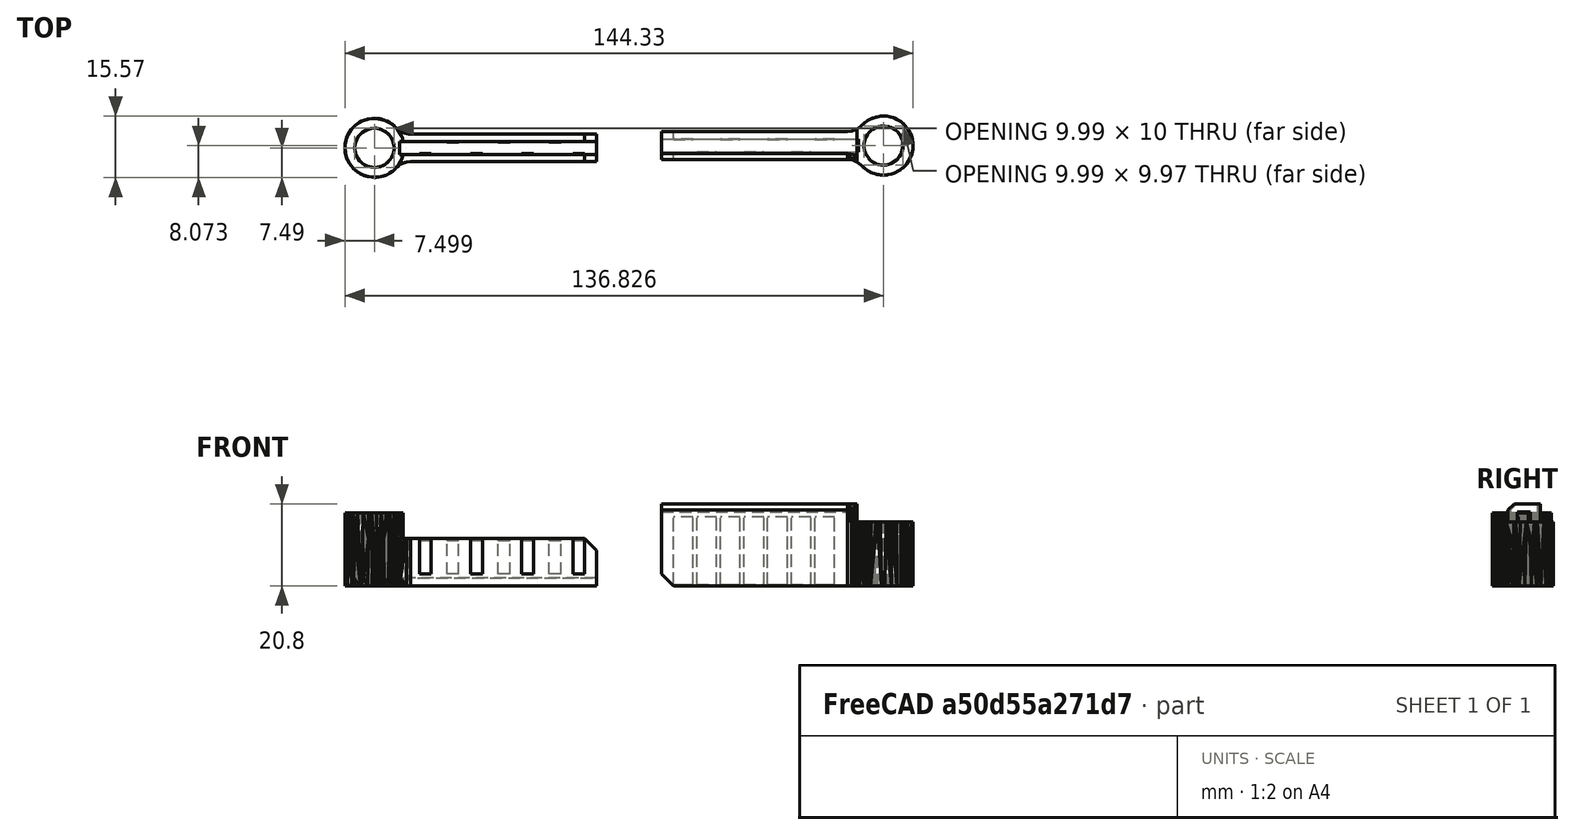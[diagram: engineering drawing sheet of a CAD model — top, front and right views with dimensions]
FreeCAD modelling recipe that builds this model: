
FCSTD DOCUMENT  (FreeCAD 0.18R14555 (Git shallow))
Label: hingle
License: All rights reserved
LicenseURL: http://en.wikipedia.org/wiki/All_rights_reserved
objects: Part::Feature×15, Part::Box×3, Part::Cut×2, Part::MultiFuse×2, Part::Chamfer×1
note: 23 computed .brp shape members not serialized (recipe doc carries the construction recipe); baked Part::Feature solids carry a one-line shape summary decoded from their .brp

FEATURE [Part::Feature] top_handle001001_solid  label="top_handle002 (Solid)"
  Placement = pos=(0,-30.81,0) rot=(0,0,1;0rad)
  shape: bbox 63.91 x 14.98 x 18.5 mm, 326 faces (baked)
FEATURE [Part::Feature] bottom_handle001001_solid  label="bottom_handle002 (Solid)"
  Placement = pos=(0,-61.62,0) rot=(0,0,1;0rad)
  shape: bbox 63.91 x 14.99 x 20.8 mm, 256 faces (baked)
FEATURE [Part::Box] Box  label="Cube"
  AttacherType = Attacher::AttachEngine3D
  Height = 21
  Length = 51
  Placement = pos=(-44.76,1.58,2) rot=(0,0,1;0rad)
  Width = 3.3
FEATURE [Part::Box] Box001  label="Cube001"
  AttacherType = Attacher::AttachEngine3D
  Height = 18.8
  Length = 61
  Placement = pos=(10.75,2.16,0) rot=(0,0,1;0rad)
  Width = 3.3
FEATURE [Part::Cut] Cut001
  Base = -> bottom_handle001001_solid
  Tool = -> Box001
FEATURE [Part::Cut] Cut
  Base = -> top_handle001001_solid
  Tool = -> Box
FEATURE [Part::Feature] Chamfer001
  shape: bbox 3 x 2 x 9 mm, 7 faces (baked)
FEATURE [Part::Feature] Chamfer002
  Placement = pos=(-13,0,0) rot=(0,0,1;0rad)
  shape: bbox 3 x 2 x 9 mm, 7 faces (baked)
FEATURE [Part::Feature] Chamfer003
  Placement = pos=(-26,0,0) rot=(0,0,1;0rad)
  shape: bbox 3 x 2 x 9 mm, 7 faces (baked)
FEATURE [Part::Feature] Chamfer004
  Placement = pos=(-39,0,0) rot=(0,0,1;0rad)
  shape: bbox 3 x 2 x 9 mm, 7 faces (baked)
FEATURE [Part::Feature] Chamfer005
  Placement = pos=(-6,0,0) rot=(0,0,1;0rad)
  shape: bbox 3 x 2 x 9 mm, 7 faces (baked)
FEATURE [Part::Feature] Chamfer006
  Placement = pos=(-19,0,0) rot=(0,0,1;0rad)
  shape: bbox 3 x 2 x 9 mm, 7 faces (baked)
FEATURE [Part::Feature] Chamfer007
  Placement = pos=(-32,0,0) rot=(0,0,1;0rad)
  shape: bbox 3 x 2 x 9 mm, 7 faces (baked)
FEATURE [Part::MultiFuse] Fusion  label="top-hingle"
  Shapes = -> [Chamfer007,Chamfer003,Chamfer005,Chamfer001,Chamfer006,Chamfer004,Chamfer002,Cut]
FEATURE [Part::Box] Box003  label="Cube003"
  AttacherType = Attacher::AttachEngine3D
  Height = 17.5
  Length = 5
  Placement = pos=(30.75,0.31,0) rot=(0,0,1;0rad)
  Width = 2
FEATURE [Part::Feature] Chamfer008 .. Chamfer011  x4 (patterned run collapsed; names and placements below)
  shape: bbox 5 x 2 x 17.5 mm, 7 faces (baked)
  placements: 4 in arithmetic series — first pos=(0,0,0) rot=(0,0,1;0rad), step (12,0,0), last pos=(36,0,0) rot=(0,0,1;0rad)
FEATURE [Part::Chamfer] Chamfer
  Base = -> Box003
  Edges = 1 edges r=0.4: [Edge11]
FEATURE [Part::Feature] Chamfer012
  Placement = pos=(12,0,0) rot=(0,0,1;0rad)
  shape: bbox 5 x 2 x 17.5 mm, 7 faces (baked)
FEATURE [Part::Feature] Chamfer013
  Placement = pos=(24,0,0) rot=(0,0,1;0rad)
  shape: bbox 5 x 2 x 17.5 mm, 7 faces (baked)
FEATURE [Part::MultiFuse] Fusion001  label="bottom-hingle"
  Shapes = -> [Chamfer013,Chamfer010,Chamfer008,Chamfer,Chamfer011,Chamfer012,Chamfer009,Cut001]
